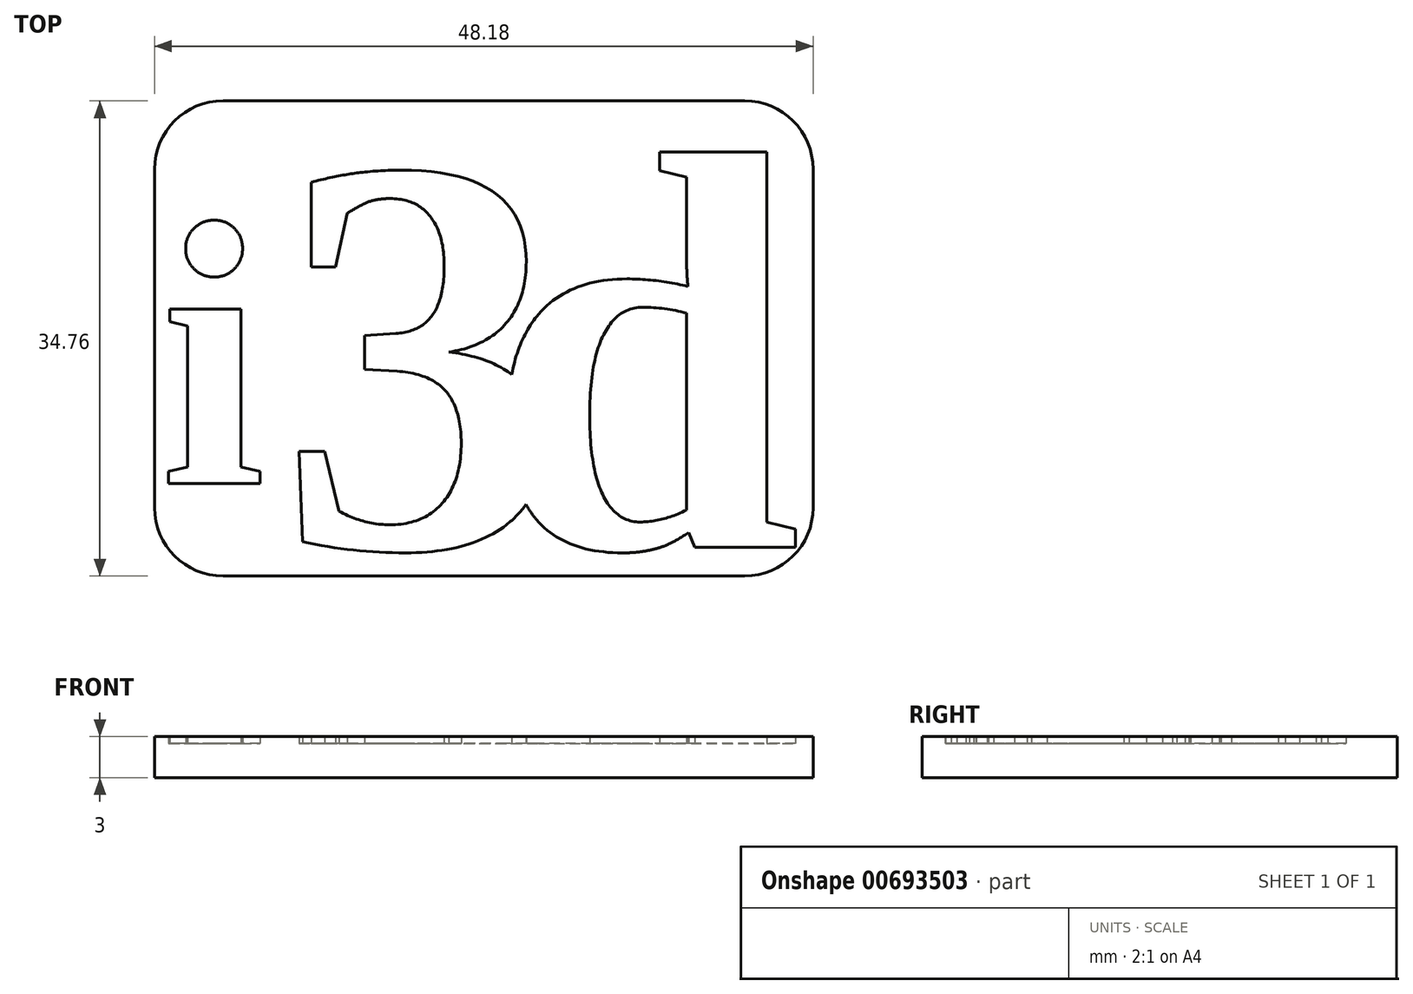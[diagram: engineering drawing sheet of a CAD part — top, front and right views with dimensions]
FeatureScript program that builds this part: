
annotation { "Feature Type Name" : "Feature", "Feature Type Description" : "" }
export const myFeature = defineFeature(function(context is Context, id is Id, definition is map)
    precondition{}
    {
        {
            var Q0;
            Q0=qCreatedBy(makeId("Top.planeOp"),FACE);
            var sketch = newSketch(context, id + "F0", { "sketchPlane" : qUnion([Q0])});
            skText(sketch, "E0", { "text": "i", "fontName": "Tinos-Bold.ttf"});
            skText(sketch, "E1", { "text": "3", "fontName": "Tinos-Bold.ttf"});
            skText(sketch, "E2", { "text": "d", "fontName": "Tinos-Bold.ttf"});
            skLineSegment(sketch, "E3.bottom", {"start": v(12.52, 26.06) * mm, "end": v(-25.66, 26.06) * mm});
            skLineSegment(sketch, "E3.top", {"start": v(12.52, -8.7) * mm, "end": v(-25.66, -8.7) * mm});
            skLineSegment(sketch, "E3.left", {"start": v(17.52, 21.06) * mm, "end": v(17.52, -3.7) * mm});
            skLineSegment(sketch, "E3.right", {"start": v(-30.66, 21.06) * mm, "end": v(-30.66, -3.7) * mm});
            skPoint(sketch, "E4.visualSharp", {"position": v(-30.66, 26.06) * mm});
            skArc(sketch, "E4.filletArc", {"start": v(-25.66, 26.06) * mm, "mid": v(-29.2, 24.6) * mm, "end": v(-30.66, 21.06) * mm});
            skPoint(sketch, "E5.visualSharp", {"position": v(17.52, 26.06) * mm});
            skArc(sketch, "E5.filletArc", {"start": v(17.52, 21.06) * mm, "mid": v(16.06, 24.6) * mm, "end": v(12.52, 26.06) * mm});
            skPoint(sketch, "E6.visualSharp", {"position": v(17.52, -8.7) * mm});
            skArc(sketch, "E6.filletArc", {"start": v(12.52, -8.7) * mm, "mid": v(16.06, -7.24) * mm, "end": v(17.52, -3.7) * mm});
            skPoint(sketch, "E7.visualSharp", {"position": v(-30.66, -8.7) * mm});
            skArc(sketch, "E7.filletArc", {"start": v(-30.66, -3.7) * mm, "mid": v(-29.2, -7.24) * mm, "end": v(-25.66, -8.7) * mm});
            const initialGuessF0  = {"E0": [-0.03025, -0.00194, 1, 0, 0.02], "E1": [-0.02166, -0.0066, 1, 0, 0.03], "E2": [-0.00648, -0.0066, 1, 0, 0.03]};
            skSetInitialGuess(sketch, initialGuessF0);
            skSolve(sketch);
        }
        {
            var Q0;
            Q0=makeQuery(id+"F0.imprint","IMPRINT",FACE,{"disambiguationData":[TD([[makeQuery(id+"F0.imprint","IMPRINT",EDGE,{"derivedFrom":sQuery(id+"F0.wireOp",EDGE,"E0.sketch_text.stroke-0")}),1.0]])]});
            var Q1;
            Q1=makeQuery(id+"F0.imprint","IMPRINT",FACE,{"disambiguationData":[TD([[makeQuery(id+"F0.imprint","IMPRINT",EDGE,{"derivedFrom":sQuery(id+"F0.wireOp",EDGE,"E2.sketch_text.stroke-18")}),1.0]])]});
            extrude(context, id + "F1", {"entities" : qUnion([Q0, Q1]), "depth" : 3 * mm, "offsetDistance" : 25 * mm});
        }
        {
            var Q0;
            Q0=makeQuery(id+"F0.imprint","IMPRINT",FACE,{"disambiguationData":[TD([[makeQuery(id+"F0.imprint","IMPRINT",EDGE,{"derivedFrom":sQuery(id+"F0.wireOp",EDGE,"E0.sketch_text.stroke-0")}),-1.0]])]});
            var Q1;
            Q1=makeQuery(id+"F0.imprint","IMPRINT",FACE,{"disambiguationData":[TD([[makeQuery(id+"F0.imprint","IMPRINT",EDGE,{"derivedFrom":sQuery(id+"F0.wireOp",EDGE,"E0.sketch_text.stroke-10")}),-1.0]])]});
            var Q2;
            {var subQ0=sQuery(id+"F0.wireOp",EDGE,"E1.sketch_text.stroke-1");Q2=makeQuery(id+"F0.imprint","IMPRINT",FACE,{"disambiguationData":[TD([[makeQuery(id+"F0.imprint","IMPRINT",EDGE,{"derivedFrom":subQ0}),-1.0]])]});}
            var Q3;
            {var subQ0=sQuery(id+"F0.wireOp",EDGE,"E1.sketch_text.stroke-28");var subQ1=sQuery(id+"F0.wireOp",EDGE,"E1.sketch_text.stroke-0");var subQ2=makeQuery(id+"F0.imprint","INTERSECT",VERTEX,{"derivedFrom":[subQ1,subQ0]});Q3=makeQuery(id+"F0.imprint","IMPRINT",FACE,{"disambiguationData":[TD([[makeQuery(id+"F0.imprint","IMPRINT",EDGE,{"disambiguationData":[TD([[subQ2,-1.0]])],"derivedFrom":subQ1}),-1.0]])]});}
            var Q4;
            Q4=makeQuery(id+"F0.imprint","IMPRINT",FACE,{"disambiguationData":[TD([[makeQuery(id+"F0.imprint","IMPRINT",EDGE,{"derivedFrom":sQuery(id+"F0.wireOp",EDGE,"E2.sketch_text.stroke-0")}),-1.0]])]});
            extrude(context, id + "F2", {"entities" : qUnion([Q0, Q1, Q2, Q3, Q4]), "operationType" : NewBodyOperationType.ADD, "depth" : 2.5 * mm, "offsetDistance" : 25 * mm});
        }
    });
